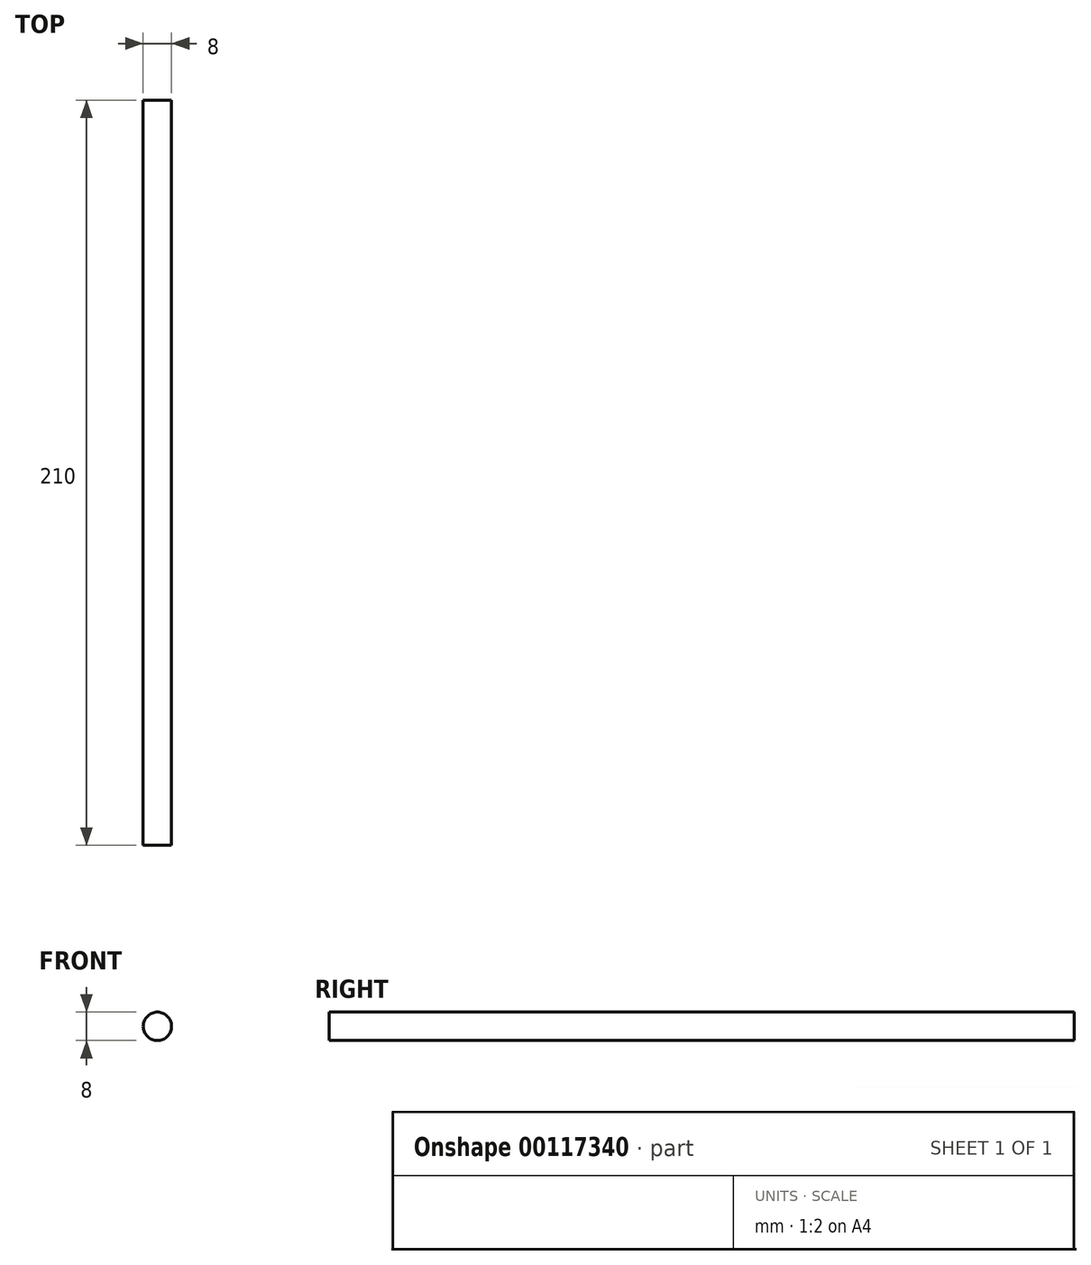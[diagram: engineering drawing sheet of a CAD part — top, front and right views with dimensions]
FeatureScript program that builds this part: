
annotation { "Feature Type Name" : "Feature", "Feature Type Description" : "" }
export const myFeature = defineFeature(function(context is Context, id is Id, definition is map)
    precondition{}
    {
        {
            var Q0;
            Q0=qCreatedBy(makeId("Front.planeOp"),FACE);
            var sketch = newSketch(context, id + "F0", { "sketchPlane" : qUnion([Q0])});
            skCircle(sketch, "E0", {"center": v(0, 0) * mm, "radius": 4 * mm});
            skSolve(sketch);
        }
        {
            var Q0;
            Q0 = qSketchRegion(id + "F0", true);
            extrude(context, id + "F1", {"entities" : qUnion([Q0]), "depth" : 210 * mm});
        }
    });
